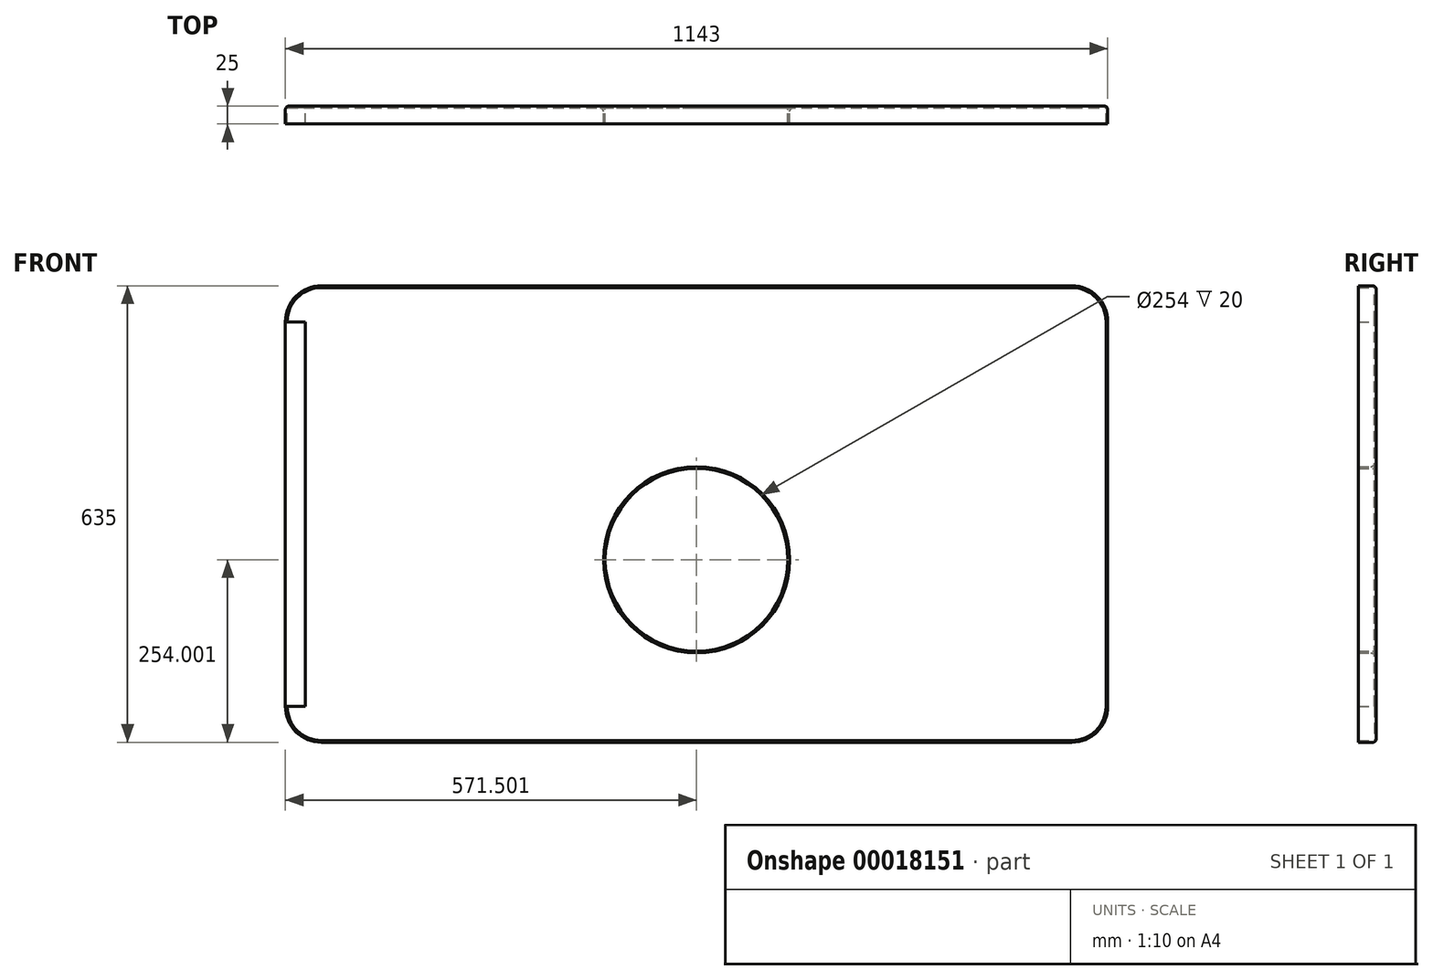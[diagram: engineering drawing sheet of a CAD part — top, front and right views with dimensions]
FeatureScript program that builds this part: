
annotation { "Feature Type Name" : "Feature", "Feature Type Description" : "" }
export const myFeature = defineFeature(function(context is Context, id is Id, definition is map)
    precondition{}
    {
        {
            var Q0;
            Q0=qCreatedBy(makeId("Front.planeOp"),FACE);
            var sketch = newSketch(context, id + "F0", { "sketchPlane" : qUnion([Q0])});
            skLineSegment(sketch, "E0", {"start": v(-575.66, 100.36) * mm, "end": v(-575.66, -434.64) * mm});
            skLineSegment(sketch, "E1", {"start": v(-525.66, -484.64) * mm, "end": v(517.34, -484.64) * mm});
            skLineSegment(sketch, "E2", {"start": v(567.34, -434.64) * mm, "end": v(567.34, 100.36) * mm});
            skLineSegment(sketch, "E3", {"start": v(517.34, 150.36) * mm, "end": v(-525.66, 150.36) * mm});
            skCircle(sketch, "E4", {"center": v(-4.16, -230.64) * mm, "radius": 127 * mm});
            skPoint(sketch, "E5.visualSharp", {"position": v(-575.66, 150.36) * mm});
            skArc(sketch, "E5.filletArc", {"start": v(-525.66, 150.36) * mm, "mid": v(-561.01, 135.72) * mm, "end": v(-575.66, 100.36) * mm});
            skPoint(sketch, "E6.visualSharp", {"position": v(-575.66, -484.64) * mm});
            skArc(sketch, "E6.filletArc", {"start": v(-575.66, -434.64) * mm, "mid": v(-561.01, -470) * mm, "end": v(-525.66, -484.64) * mm});
            skPoint(sketch, "E7.visualSharp", {"position": v(567.34, -484.64) * mm});
            skArc(sketch, "E7.filletArc", {"start": v(517.34, -484.64) * mm, "mid": v(552.7, -470) * mm, "end": v(567.34, -434.64) * mm});
            skPoint(sketch, "E8.visualSharp", {"position": v(567.34, 150.36) * mm});
            skArc(sketch, "E8.filletArc", {"start": v(567.34, 100.36) * mm, "mid": v(552.7, 135.72) * mm, "end": v(517.34, 150.36) * mm});
            skSolve(sketch);
        }
        {
            var Q0;
            Q0 = qSketchRegion(id + "F0", true);
            extrude(context, id + "F1", {"entities" : qUnion([Q0]), "depth" : 25 * mm});
        }
        {
            var Q0;
            Q0=makeQuery(id+"F1.opExtrude","CAP_FACE",FACE,{"disambiguationData":[OSD([sQuery(id+"F0.wireOp",EDGE,"E0"),sQuery(id+"F0.wireOp",EDGE,"E1"),sQuery(id+"F0.wireOp",EDGE,"E2"),sQuery(id+"F0.wireOp",EDGE,"E3"),sQuery(id+"F0.wireOp",EDGE,"E4"),sQuery(id+"F0.wireOp",EDGE,"E5.filletArc"),sQuery(id+"F0.wireOp",EDGE,"E6.filletArc"),sQuery(id+"F0.wireOp",EDGE,"E7.filletArc"),sQuery(id+"F0.wireOp",EDGE,"E8.filletArc")])],"isStart":false});
            shell(context, id + "F2", {"entities" : qUnion([Q0]), "thickness" : 2.5 * mm});
        }
        {
            var Q0;
            Q0=makeQuery(id+"F1.opExtrude","CAP_EDGE",EDGE,{"disambiguationData":[OSD([sQuery(id+"F0.wireOp",EDGE,"E4")])],"isStart":true});
            fillet(context, id + "F3", {"entities" : qUnion([Q0]), "radius" : 5 * mm, "tangentPropagation" : true, "allowEdgeOverflow" : false});
        }
        {
            var Q0;
            {var subQ0=sQuery(id+"F0.wireOp",EDGE,"E4");Q0=makeQuery(id+"F2.opShell","OFFSET_EDGE",EDGE,{"disambiguationData":[OSD([subQ0]),TDD([makeQuery(id+"F1.opExtrude","CAP_EDGE",EDGE,{"disambiguationData":[OSD([subQ0])],"isStart":true})])]});}
            fillet(context, id + "F4", {"entities" : qUnion([Q0]), "radius" : 5 * mm, "tangentPropagation" : true, "allowEdgeOverflow" : false});
        }
        {
            var Q0;
            Q0=makeQuery(id+"F1.opExtrude","CAP_EDGE",EDGE,{"disambiguationData":[OSD([sQuery(id+"F0.wireOp",EDGE,"E2")])],"isStart":true});
            var Q1;
            Q1=makeQuery(id+"F1.opExtrude","CAP_EDGE",EDGE,{"disambiguationData":[OSD([sQuery(id+"F0.wireOp",EDGE,"E8.filletArc")])],"isStart":true});
            var Q2;
            Q2=makeQuery(id+"F1.opExtrude","CAP_EDGE",EDGE,{"disambiguationData":[OSD([sQuery(id+"F0.wireOp",EDGE,"E3")])],"isStart":true});
            var Q3;
            Q3=makeQuery(id+"F1.opExtrude","CAP_EDGE",EDGE,{"disambiguationData":[OSD([sQuery(id+"F0.wireOp",EDGE,"E5.filletArc")])],"isStart":true});
            var Q4;
            Q4=makeQuery(id+"F1.opExtrude","CAP_EDGE",EDGE,{"disambiguationData":[OSD([sQuery(id+"F0.wireOp",EDGE,"E0")])],"isStart":true});
            var Q5;
            Q5=makeQuery(id+"F1.opExtrude","CAP_EDGE",EDGE,{"disambiguationData":[OSD([sQuery(id+"F0.wireOp",EDGE,"E6.filletArc")])],"isStart":true});
            var Q6;
            Q6=makeQuery(id+"F1.opExtrude","CAP_EDGE",EDGE,{"disambiguationData":[OSD([sQuery(id+"F0.wireOp",EDGE,"E1")])],"isStart":true});
            var Q7;
            Q7=makeQuery(id+"F1.opExtrude","CAP_EDGE",EDGE,{"disambiguationData":[OSD([sQuery(id+"F0.wireOp",EDGE,"E7.filletArc")])],"isStart":true});
            fillet(context, id + "F5", {"entities" : qUnion([Q0, Q1, Q2, Q3, Q4, Q5, Q6, Q7]), "radius" : 5 * mm, "tangentPropagation" : true, "allowEdgeOverflow" : false});
        }
        {
            var Q0;
            Q0=makeQuery(id+"F2.opShell","OFFSET_FACE",FACE,{"disambiguationData":[OSD([sQuery(id+"F0.wireOp",EDGE,"E0")])]});
            extrude(context, id + "F6", {"entities" : qUnion([Q0]), "operationType" : NewBodyOperationType.ADD, "depth" : 25 * mm});
        }
    });
